# Revit family: Volleyball-System_CarbonLite-Composite_VB7222
name_source: partatom
category: Specialty Equipment
revit_build: Autodesk Revit 2018 (Build: 20180423_1000(x64)
units: mm (PartAtom-declared; Revit-internal decimal feet)

## family parameters
Always vertical = Yes
Cut with Voids When Loaded = No
OmniClass Number = 23.40.50.34.24
OmniClass Title = Nets
Part Type = Normal
Room Calculation Point = No
Round Connector Dimension = Use Diameter
Shared = No
Work Plane-Based = Yes

## types (1)
- as Specified
    Assembly Code = E1090
    Building Codes = https://www.brpbybison.com
    Center to Center Posts = 37' - 0"
    Construction Details = https://www.arcat.com
    Default Elevation = 0' - 0"
    Description = IPI by Bison Gymnasium Equipment
    Expected Lifespan (Years) = 0
    Green Building-LEED = https://www.arcat.com
    Installation-Fabrication = http://www.ipibybison.com
    Keynote = 11 66 00
    Maintenance Schedule (Months) = 0
    Manufacturer = BRP by bison
    Manufacturer Fax = 888-438-5312
    Manufacturer Website = http://www.ipibybison.com
    Model = As Specified
    Product Data = http://www.arcat.com
    Product Properties = http://www.ipibybison.com
    Revision = R1_2018-09
    Sales Information = http://www.ipibybison.com
    SpecWizard = https://www.arcat.com
    Specification = https://www.arcat.com
    Standards Conformance = as Specified
    Test Data = http://www.ipibybison.com
    URL = https://ipibybison.com
    Warranty Duration (Years) = 0

## geometry (parser evidence)
native form markers: Sweep x3
no freeform markers — native parametric forms only
